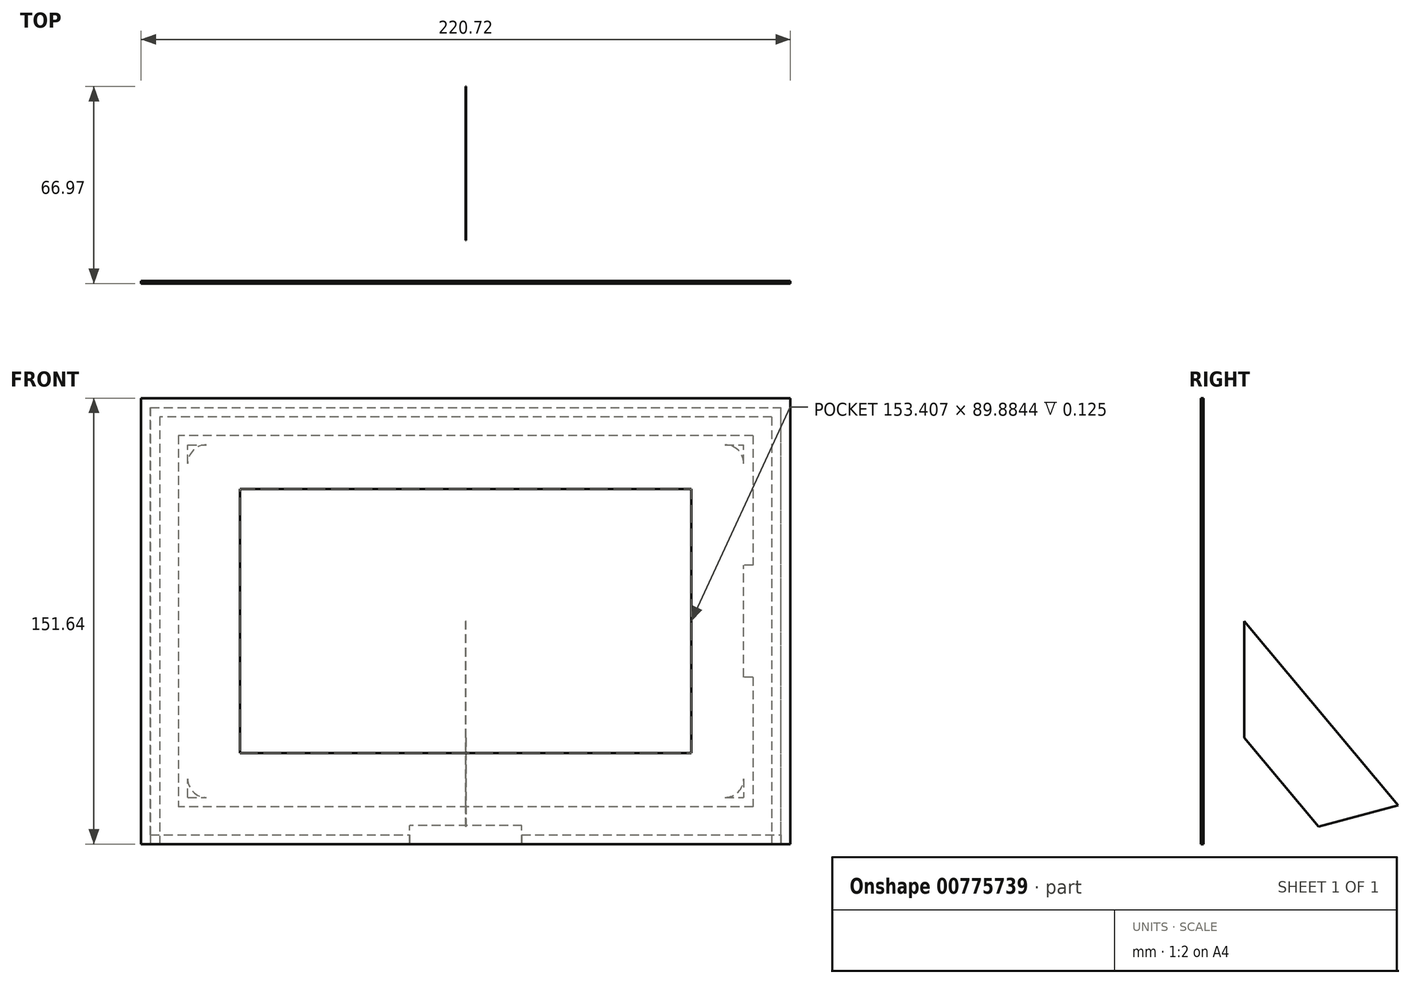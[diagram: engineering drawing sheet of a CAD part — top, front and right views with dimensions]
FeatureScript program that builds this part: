
annotation { "Feature Type Name" : "Feature", "Feature Type Description" : "" }
export const myFeature = defineFeature(function(context is Context, id is Id, definition is map)
    precondition{}
    {
        {
            assignVariable(context, id + "F0", {"name" : "sheetThickness", "anyValue" : 1 / 8});
        }
        {
            assignVariable(context, id + "F1", {"name" : "tabletZ", "anyValue" : 0.45});
        }
        {
            var Q0;
            Q0=qCreatedBy(makeId("Front.planeOp"),FACE);
            var sketch = newSketch(context, id + "F2", { "sketchPlane" : qUnion([Q0])});
            skLineSegment(sketch, "E0.bottom", {"start": v(88.14, -59.94) * mm, "end": v(-88.14, -59.94) * mm});
            skLineSegment(sketch, "E0.top", {"start": v(88.14, 59.94) * mm, "end": v(-88.14, 59.94) * mm});
            skLineSegment(sketch, "E0.left", {"start": v(94.49, -53.6) * mm, "end": v(94.49, 53.6) * mm});
            skLineSegment(sketch, "E0.right", {"start": v(-94.49, -53.6) * mm, "end": v(-94.49, 53.6) * mm});
            skPoint(sketch, "E0.middle", {"position": v(0, 0) * mm});
            skLineSegment(sketch, "E1.bottom", {"start": v(-76.7, 44.94) * mm, "end": v(76.7, 44.94) * mm});
            skLineSegment(sketch, "E1.top", {"start": v(-76.7, -44.94) * mm, "end": v(76.7, -44.94) * mm});
            skLineSegment(sketch, "E1.left", {"start": v(-76.7, 44.94) * mm, "end": v(-76.7, -44.94) * mm});
            skLineSegment(sketch, "E1.right", {"start": v(76.7, 44.94) * mm, "end": v(76.7, -44.94) * mm});
            skLineSegment(sketch, "E2", {"start": v(-76.7, 44.94) * mm, "end": v(76.7, -44.94) * mm, "construction": true});
            skPoint(sketch, "E3.visualSharp", {"position": v(-94.49, 59.94) * mm});
            skArc(sketch, "E3.filletArc", {"start": v(-88.14, 59.94) * mm, "mid": v(-92.63, 58.08) * mm, "end": v(-94.49, 53.6) * mm});
            skPoint(sketch, "E4.visualSharp", {"position": v(94.49, 59.94) * mm});
            skArc(sketch, "E4.filletArc", {"start": v(94.49, 53.6) * mm, "mid": v(92.63, 58.08) * mm, "end": v(88.14, 59.94) * mm});
            skPoint(sketch, "E5.visualSharp", {"position": v(94.49, -59.94) * mm});
            skArc(sketch, "E5.filletArc", {"start": v(88.14, -59.94) * mm, "mid": v(92.63, -58.08) * mm, "end": v(94.49, -53.6) * mm});
            skPoint(sketch, "E6.visualSharp", {"position": v(-94.49, -59.94) * mm});
            skArc(sketch, "E6.filletArc", {"start": v(-94.49, -53.6) * mm, "mid": v(-92.63, -58.08) * mm, "end": v(-88.14, -59.94) * mm});
            skLineSegment(sketch, "E7.bottom", {"start": v(110.36, -75.82) * mm, "end": v(-110.36, -75.82) * mm});
            skLineSegment(sketch, "E7.top", {"start": v(110.36, 75.82) * mm, "end": v(-110.36, 75.82) * mm});
            skLineSegment(sketch, "E7.left", {"start": v(110.36, -75.82) * mm, "end": v(110.36, 75.82) * mm});
            skLineSegment(sketch, "E7.right", {"start": v(-110.36, -75.82) * mm, "end": v(-110.36, 75.82) * mm});
            skLineSegment(sketch, "E8.bottom", {"start": v(-107.19, -72.64) * mm, "end": v(107.19, -72.64) * mm});
            skLineSegment(sketch, "E8.top", {"start": v(-107.19, 72.64) * mm, "end": v(107.19, 72.64) * mm});
            skLineSegment(sketch, "E8.left", {"start": v(-107.19, -72.64) * mm, "end": v(-107.19, 72.64) * mm});
            skLineSegment(sketch, "E8.right", {"start": v(107.19, -72.64) * mm, "end": v(107.19, 72.64) * mm});
            skLineSegment(sketch, "E9", {"start": v(107.19, -72.64) * mm, "end": v(107.19, -75.82) * mm});
            skLineSegment(sketch, "E10", {"start": v(-107.19, -72.64) * mm, "end": v(-107.19, -75.82) * mm});
            skLineSegment(sketch, "E11", {"start": v(107.19, 72.64) * mm, "end": v(107.19, 75.82) * mm});
            skLineSegment(sketch, "E12", {"start": v(-107.19, 72.64) * mm, "end": v(-107.19, 75.82) * mm});
            skLineSegment(sketch, "E13.bottom", {"start": v(97.66, 63.12) * mm, "end": v(-97.66, 63.12) * mm});
            skLineSegment(sketch, "E13.top", {"start": v(97.66, -63.12) * mm, "end": v(-97.66, -63.12) * mm});
            skLineSegment(sketch, "E13.left", {"start": v(97.66, 63.12) * mm, "end": v(97.66, -63.12) * mm});
            skLineSegment(sketch, "E13.right", {"start": v(-97.66, 63.12) * mm, "end": v(-97.66, -63.12) * mm});
            skLineSegment(sketch, "E14.bottom", {"start": v(94.49, 59.94) * mm, "end": v(-94.49, 59.94) * mm});
            skLineSegment(sketch, "E14.top", {"start": v(94.49, -59.94) * mm, "end": v(-94.49, -59.94) * mm});
            skLineSegment(sketch, "E14.left", {"start": v(94.49, 59.94) * mm, "end": v(94.49, -59.94) * mm});
            skLineSegment(sketch, "E14.right", {"start": v(-94.49, 59.94) * mm, "end": v(-94.49, -59.94) * mm});
            skLineSegment(sketch, "E15", {"start": v(94.49, 0) * mm, "end": v(97.66, 0) * mm, "construction": true});
            skLineSegment(sketch, "E16", {"start": v(97.66, 19.05) * mm, "end": v(94.49, 19.05) * mm});
            skLineSegment(sketch, "E17", {"start": v(97.66, -19.05) * mm, "end": v(94.49, -19.05) * mm});
            skLineSegment(sketch, "E18", {"start": v(0, -72.64) * mm, "end": v(0, -75.82) * mm, "construction": true});
            skLineSegment(sketch, "E19", {"start": v(19.05, -72.64) * mm, "end": v(19.05, -75.82) * mm});
            skLineSegment(sketch, "E20", {"start": v(-19.05, -72.64) * mm, "end": v(-19.05, -75.82) * mm});
            skSolve(sketch);
        }
        {
            var Q0;
            Q0=makeQuery(id+"F2.imprint","IMPRINT",FACE,{"disambiguationData":[TD([[makeQuery(id+"F2.imprint","IMPRINT",EDGE,{"derivedFrom":sQuery(id+"F2.wireOp",EDGE,"E1.bottom")}),-1.0]])]});
            var Q1;
            Q1=makeQuery(id+"F2.imprint","IMPRINT",FACE,{"disambiguationData":[TD([[makeQuery(id+"F2.imprint","IMPRINT",EDGE,{"derivedFrom":sQuery(id+"F2.wireOp",EDGE,"E1.bottom")}),1.0]])]});
            extrude(context, id + "F3", {"entities" : qUnion([Q0, Q1]), "oppositeDirection" : true, "depth" : (getVariable(context, 'tabletZ')) * mm, "offsetDistance" : 25.4 * mm});
        }
        {
            var Q0;
            Q0=makeQuery(id+"F2.imprint","IMPRINT",FACE,{"disambiguationData":[TD([[makeQuery(id+"F2.imprint","IMPRINT",EDGE,{"derivedFrom":sQuery(id+"F2.wireOp",EDGE,"E8.top")}),1.0]])]});
            var Q1;
            {var subQ0=sQuery(id+"F2.wireOp",EDGE,"E7.right");Q1=makeQuery(id+"F2.imprint","IMPRINT",FACE,{"disambiguationData":[TD([[makeQuery(id+"F2.imprint","IMPRINT",EDGE,{"derivedFrom":subQ0}),-1.0]])]});}
            var Q2;
            Q2=makeQuery(id+"F2.imprint","IMPRINT",FACE,{"disambiguationData":[TD([[makeQuery(id+"F2.imprint","IMPRINT",EDGE,{"derivedFrom":sQuery(id+"F2.wireOp",EDGE,"E8.bottom")}),-1.0]])]});
            var Q3;
            {var subQ0=sQuery(id+"F2.wireOp",EDGE,"E7.left");Q3=makeQuery(id+"F2.imprint","IMPRINT",FACE,{"disambiguationData":[TD([[makeQuery(id+"F2.imprint","IMPRINT",EDGE,{"derivedFrom":subQ0}),1.0]])]});}
            var Q4;
            Q4=makeQuery(id+"F2.imprint","IMPRINT",FACE,{"disambiguationData":[TD([[makeQuery(id+"F2.imprint","IMPRINT",EDGE,{"derivedFrom":sQuery(id+"F2.wireOp",EDGE,"E8.bottom")}),1.0]])]});
            var Q5;
            {var subQ15=sQuery(id+"F2.wireOp",EDGE,"E13.bottom");Q5=makeQuery(id+"F2.imprint","IMPRINT",FACE,{"disambiguationData":[TD([[makeQuery(id+"F2.imprint","IMPRINT",EDGE,{"derivedFrom":subQ15}),1.0]])]});}
            var Q6;
            {var subQ0=sQuery(id+"F2.wireOp",EDGE,"E16");Q6=makeQuery(id+"F2.imprint","IMPRINT",FACE,{"disambiguationData":[TD([[makeQuery(id+"F2.imprint","IMPRINT",EDGE,{"derivedFrom":subQ0}),1.0]])]});}
            var Q7;
            Q7=makeQuery(id+"F2.imprint","IMPRINT",FACE,{"disambiguationData":[TD([[makeQuery(id+"F2.imprint","IMPRINT",EDGE,{"derivedFrom":sQuery(id+"F2.wireOp",EDGE,"E1.bottom")}),1.0]])]});
            var Q8;
            {var subQ0=sQuery(id+"F2.wireOp",EDGE,"E3.filletArc");Q8=makeQuery(id+"F2.imprint","IMPRINT",FACE,{"disambiguationData":[TD([[makeQuery(id+"F2.imprint","IMPRINT",EDGE,{"derivedFrom":subQ0}),-1.0]])]});}
            var Q9;
            {var subQ0=sQuery(id+"F2.wireOp",EDGE,"E6.filletArc");Q9=makeQuery(id+"F2.imprint","IMPRINT",FACE,{"disambiguationData":[TD([[makeQuery(id+"F2.imprint","IMPRINT",EDGE,{"derivedFrom":subQ0}),-1.0]])]});}
            var Q10;
            {var subQ0=sQuery(id+"F2.wireOp",EDGE,"E5.filletArc");Q10=makeQuery(id+"F2.imprint","IMPRINT",FACE,{"disambiguationData":[TD([[makeQuery(id+"F2.imprint","IMPRINT",EDGE,{"derivedFrom":subQ0}),-1.0]])]});}
            var Q11;
            {var subQ0=sQuery(id+"F2.wireOp",EDGE,"E4.filletArc");Q11=makeQuery(id+"F2.imprint","IMPRINT",FACE,{"disambiguationData":[TD([[makeQuery(id+"F2.imprint","IMPRINT",EDGE,{"derivedFrom":subQ0}),-1.0]])]});}
            extrude(context, id + "F4", {"entities" : qUnion([Q0, Q1, Q2, Q3, Q4, Q5, Q6, Q7, Q8, Q9, Q10, Q11]), "depth" : (getVariable(context, 'sheetThickness')) * mm, "offsetDistance" : 25.4 * mm});
        }
        {
            var Q0;
            {var subQ15=sQuery(id+"F2.wireOp",EDGE,"E13.bottom");Q0=makeQuery(id+"F2.imprint","IMPRINT",FACE,{"disambiguationData":[TD([[makeQuery(id+"F2.imprint","IMPRINT",EDGE,{"derivedFrom":subQ15}),1.0]])]});}
            var Q1;
            Q1=makeQuery(id+"F3.opExtrude","CAP_FACE",FACE,{"disambiguationData":[OSD([sQuery(id+"F2.wireOp",EDGE,"E3.filletArc"),sQuery(id+"F2.wireOp",EDGE,"E4.filletArc"),sQuery(id+"F2.wireOp",EDGE,"E5.filletArc"),sQuery(id+"F2.wireOp",EDGE,"E6.filletArc"),sQuery(id+"F2.wireOp",EDGE,"E14.bottom"),sQuery(id+"F2.wireOp",EDGE,"E14.top"),sQuery(id+"F2.wireOp",EDGE,"E14.left"),sQuery(id+"F2.wireOp",EDGE,"E14.right")])],"isStart":false});
            extrude(context, id + "F5", {"entities" : qUnion([Q0]), "operationType" : NewBodyOperationType.ADD, "endBound" : BoundingType.UP_TO_SURFACE, "oppositeDirection" : true, "depth" : 25.4 * mm, "endBoundEntityFace" : qUnion([Q1]), "offsetDistance" : 25.4 * mm});
        }
        {
            var Q0;
            Q0=makeQuery(id+"F2.imprint","IMPRINT",FACE,{"disambiguationData":[TD([[makeQuery(id+"F2.imprint","IMPRINT",EDGE,{"derivedFrom":sQuery(id+"F2.wireOp",EDGE,"E8.top")}),1.0]])]});
            var Q1;
            {var subQ0=sQuery(id+"F2.wireOp",EDGE,"E7.left");Q1=makeQuery(id+"F2.imprint","IMPRINT",FACE,{"disambiguationData":[TD([[makeQuery(id+"F2.imprint","IMPRINT",EDGE,{"derivedFrom":subQ0}),1.0]])]});}
            var Q2;
            {var subQ0=sQuery(id+"F2.wireOp",EDGE,"E7.right");Q2=makeQuery(id+"F2.imprint","IMPRINT",FACE,{"disambiguationData":[TD([[makeQuery(id+"F2.imprint","IMPRINT",EDGE,{"derivedFrom":subQ0}),-1.0]])]});}
            var Q3;
            {var subQ0=sQuery(id+"F2.wireOp",EDGE,"E10");Q3=makeQuery(id+"F2.imprint","IMPRINT",FACE,{"disambiguationData":[TD([[makeQuery(id+"F2.imprint","IMPRINT",EDGE,{"derivedFrom":subQ0}),1.0]])]});}
            var Q4;
            {var subQ0=sQuery(id+"F2.wireOp",EDGE,"E9");Q4=makeQuery(id+"F2.imprint","IMPRINT",FACE,{"disambiguationData":[TD([[makeQuery(id+"F2.imprint","IMPRINT",EDGE,{"derivedFrom":subQ0}),-1.0]])]});}
            extrude(context, id + "F6", {"entities" : qUnion([Q0, Q1, Q2, Q3, Q4]), "operationType" : NewBodyOperationType.ADD, "oppositeDirection" : true, "depth" : (getVariable(context, 'tabletZ') + getVariable(context, 'sheetThickness')) * mm, "offsetDistance" : 25.4 * mm});
        }
        {
            var Q0;
            Q0=makeQuery(id+"F6.opExtrude","CAP_FACE",FACE,{"disambiguationData":[OSD([sQuery(id+"F2.wireOp",EDGE,"E7.bottom"),sQuery(id+"F2.wireOp",EDGE,"E7.top"),sQuery(id+"F2.wireOp",EDGE,"E7.left"),sQuery(id+"F2.wireOp",EDGE,"E7.right"),sQuery(id+"F2.wireOp",EDGE,"E8.bottom"),sQuery(id+"F2.wireOp",EDGE,"E8.top"),sQuery(id+"F2.wireOp",EDGE,"E8.left"),sQuery(id+"F2.wireOp",EDGE,"E8.right"),sQuery(id+"F2.wireOp",EDGE,"E19"),sQuery(id+"F2.wireOp",EDGE,"E20")])],"isStart":false});
            var sketch = newSketch(context, id + "F7", { "sketchPlane" : qUnion([Q0])});
            skLineSegment(sketch, "E21.0", {"start": v(-110.36, 75.82) * mm, "end": v(110.36, 75.82) * mm});
            skLineSegment(sketch, "E22.0", {"start": v(-110.36, -75.82) * mm, "end": v(-110.36, 75.82) * mm});
            skLineSegment(sketch, "E23.0", {"start": v(-110.36, -75.82) * mm, "end": v(110.36, -75.82) * mm});
            skLineSegment(sketch, "E24.0", {"start": v(110.36, -75.82) * mm, "end": v(110.36, 75.82) * mm});
            skLineSegment(sketch, "E25", {"start": v(-104.01, 69.47) * mm, "end": v(-104.01, -75.82) * mm});
            skLineSegment(sketch, "E26", {"start": v(-104.01, 69.47) * mm, "end": v(104.01, 69.47) * mm});
            skLineSegment(sketch, "E27", {"start": v(104.01, 69.47) * mm, "end": v(104.01, -75.82) * mm});
            skLineSegment(sketch, "E28.0", {"start": v(-19.05, -72.64) * mm, "end": v(-107.19, -72.64) * mm});
            skLineSegment(sketch, "E29.0", {"start": v(-19.05, -72.64) * mm, "end": v(-19.05, -75.82) * mm});
            skLineSegment(sketch, "E30.0", {"start": v(19.05, -72.64) * mm, "end": v(19.05, -75.82) * mm});
            skLineSegment(sketch, "E31.0", {"start": v(107.19, -72.64) * mm, "end": v(19.05, -72.64) * mm});
            skLineSegment(sketch, "E32", {"start": v(107.19, -72.64) * mm, "end": v(107.19, -75.82) * mm});
            skLineSegment(sketch, "E33", {"start": v(-107.19, -72.64) * mm, "end": v(-107.19, -75.82) * mm});
            skSolve(sketch);
        }
        {
            var Q0;
            Q0=makeQuery(id+"F7.imprint","IMPRINT",FACE,{"disambiguationData":[TD([[makeQuery(id+"F7.imprint","IMPRINT",EDGE,{"derivedFrom":sQuery(id+"F7.wireOp",EDGE,"E21.0")}),-1.0]])]});
            var Q1;
            {var subQ1=sQuery(id+"F7.wireOp",EDGE,"E26");Q1=makeQuery(id+"F7.imprint","IMPRINT",FACE,{"disambiguationData":[TD([[makeQuery(id+"F7.imprint","IMPRINT",EDGE,{"derivedFrom":subQ1}),1.0]])]});}
            var Q2;
            {var subQ3=sQuery(id+"F7.wireOp",EDGE,"E32");Q2=makeQuery(id+"F7.imprint","IMPRINT",FACE,{"disambiguationData":[TD([[makeQuery(id+"F7.imprint","IMPRINT",EDGE,{"derivedFrom":subQ3}),-1.0]])]});}
            var Q3;
            {var subQ3=sQuery(id+"F7.wireOp",EDGE,"E33");Q3=makeQuery(id+"F7.imprint","IMPRINT",FACE,{"disambiguationData":[TD([[makeQuery(id+"F7.imprint","IMPRINT",EDGE,{"derivedFrom":subQ3}),1.0]])]});}
            extrude(context, id + "F8", {"entities" : qUnion([Q0, Q1, Q2, Q3]), "depth" : (getVariable(context, 'sheetThickness')) * mm, "offsetDistance" : 25.4 * mm});
        }
        {
            var Q0;
            {var subQ3=sQuery(id+"F7.wireOp",EDGE,"E33");Q0=makeQuery(id+"F7.imprint","IMPRINT",FACE,{"disambiguationData":[TD([[makeQuery(id+"F7.imprint","IMPRINT",EDGE,{"derivedFrom":subQ3}),1.0]])]});}
            var Q1;
            {var subQ0=sQuery(id+"F7.wireOp",EDGE,"E29.0");Q1=makeQuery(id+"F7.imprint","IMPRINT",FACE,{"disambiguationData":[TD([[makeQuery(id+"F7.imprint","IMPRINT",EDGE,{"derivedFrom":subQ0}),-1.0]])]});}
            var Q2;
            {var subQ0=sQuery(id+"F7.wireOp",EDGE,"E30.0");Q2=makeQuery(id+"F7.imprint","IMPRINT",FACE,{"disambiguationData":[TD([[makeQuery(id+"F7.imprint","IMPRINT",EDGE,{"derivedFrom":subQ0}),1.0]])]});}
            var Q3;
            {var subQ3=sQuery(id+"F7.wireOp",EDGE,"E32");Q3=makeQuery(id+"F7.imprint","IMPRINT",FACE,{"disambiguationData":[TD([[makeQuery(id+"F7.imprint","IMPRINT",EDGE,{"derivedFrom":subQ3}),-1.0]])]});}
            extrude(context, id + "F9", {"entities" : qUnion([Q0, Q1, Q2, Q3]), "operationType" : NewBodyOperationType.REMOVE, "oppositeDirection" : true, "depth" : (getVariable(context, 'sheetThickness')) * mm, "offsetDistance" : 25.4 * mm});
        }
        {
            var Q0;
            Q0=makeQuery(id+"F7.imprint","IMPRINT",FACE,{"disambiguationData":[TD([[makeQuery(id+"F7.imprint","IMPRINT",EDGE,{"derivedFrom":sQuery(id+"F7.wireOp",EDGE,"E21.0")}),-1.0]])]});
            var sketch = newSketch(context, id + "F10", { "sketchPlane" : qUnion([Q0])});
            skLineSegment(sketch, "E34.0", {"start": v(107.19, -75.82) * mm, "end": v(107.19, 72.64) * mm});
            skLineSegment(sketch, "E35.0", {"start": v(107.19, 72.64) * mm, "end": v(-107.19, 72.64) * mm});
            skLineSegment(sketch, "E36.0", {"start": v(-107.19, -75.82) * mm, "end": v(-107.19, 72.64) * mm});
            skLineSegment(sketch, "E37.0", {"start": v(-110.36, -75.82) * mm, "end": v(110.36, -75.82) * mm});
            skLineSegment(sketch, "E38", {"start": v(0, -75.82) * mm, "end": v(0, -69.47) * mm, "construction": true});
            skLineSegment(sketch, "E39.bottom", {"start": v(-19.05, -75.82) * mm, "end": v(19.05, -75.82) * mm, "construction": true});
            skLineSegment(sketch, "E39.top", {"start": v(-19.05, -69.47) * mm, "end": v(19.05, -69.47) * mm});
            skLineSegment(sketch, "E39.left", {"start": v(-19.05, -75.82) * mm, "end": v(-19.05, -69.47) * mm});
            skLineSegment(sketch, "E39.right", {"start": v(19.05, -75.82) * mm, "end": v(19.05, -69.47) * mm});
            skSolve(sketch);
        }
        {
            var Q0;
            {var subQ2=sQuery(id+"F10.wireOp",EDGE,"E35.0");Q0=makeQuery(id+"F10.imprint","IMPRINT",FACE,{"disambiguationData":[TD([[makeQuery(id+"F10.imprint","IMPRINT",EDGE,{"derivedFrom":subQ2}),1.0]])]});}
            extrude(context, id + "F11", {"entities" : qUnion([Q0]), "oppositeDirection" : true, "depth" : (getVariable(context, 'sheetThickness')) * mm, "offsetDistance" : 25.4 * mm});
        }
        {
            var Q0;
            Q0=qCreatedBy(makeId("Right.planeOp"),FACE);
            var sketch = newSketch(context, id + "F12", { "sketchPlane" : qUnion([Q0])});
            skLineSegment(sketch, "E40.0.0", {"start": v(14.6, -69.47) * mm, "end": v(14.6, -75.82) * mm});
            skLineSegment(sketch, "E40.0.2", {"start": v(14.6, -75.82) * mm, "end": v(14.6, -72.64) * mm});
            skLineSegment(sketch, "E40.0.3", {"start": v(14.6, -72.64) * mm, "end": v(14.6, 72.64) * mm});
            skLineSegment(sketch, "E40.0.5", {"start": v(14.6, 72.64) * mm, "end": v(14.6, -72.64) * mm});
            skLineSegment(sketch, "E40.0.6", {"start": v(14.6, -72.64) * mm, "end": v(14.6, -75.82) * mm});
            skLineSegment(sketch, "E40.0.8", {"start": v(14.6, -75.82) * mm, "end": v(14.6, -69.47) * mm});
            skLineSegment(sketch, "E41.0", {"start": v(17.78, -75.82) * mm, "end": v(14.6, -75.82) * mm});
            skLineSegment(sketch, "E42.0", {"start": v(-3.18, -75.82) * mm, "end": v(14.6, -75.82) * mm});
            skLineSegment(sketch, "E43", {"start": v(17.78, -75.82) * mm, "end": v(66.85, -62.67) * mm, "construction": true});
            skLineSegment(sketch, "E44", {"start": v(-7.02, -78.88) * mm, "end": v(45.33, -78.88) * mm, "construction": true});
            skLineSegment(sketch, "E45", {"start": v(66.85, -62.67) * mm, "end": v(14.6, 0) * mm});
            skLineSegment(sketch, "E46", {"start": v(14.6, -39.67) * mm, "end": v(39.82, -69.91) * mm});
            skLineSegment(sketch, "E47", {"start": v(39.82, -69.91) * mm, "end": v(66.85, -62.67) * mm});
            skSolve(sketch);
        }
        {
            var Q0;
            {var subQ0=sQuery(id+"F12.wireOp",EDGE,"E45");Q0=makeQuery(id+"F12.imprint","IMPRINT",FACE,{"disambiguationData":[TD([[makeQuery(id+"F12.imprint","IMPRINT",EDGE,{"derivedFrom":subQ0}),1.0]])]});}
            extrude(context, id + "F13", {"entities" : qUnion([Q0]), "operationType" : NewBodyOperationType.ADD, "endBound" : BoundingType.SYMMETRIC, "depth" : (getVariable(context, 'sheetThickness')) * mm, "offsetDistance" : 25.4 * mm});
        }
    });
